# Revit family: 2-5104-24 Apollo
name_source: partatom
category: Lighting Fixtures
revit_build: Autodesk Revit LT 2014 (Build: 20130308_1515(x64)
units: mm (PartAtom-declared; Revit-internal decimal feet)

## types (1)
- 2-5104-24 Apollo
    ADA Compliant = Yes
    Apparent Load = 31 VA
    Ballast  Manufacturer = Antron Electronics
    Color Filter = 16777215
    Default Elevation = 4' - 0"
    Description = 24 1/4" Vanity
    Diffuser = Matte White Acrylic
    Dimming Lamp Color Temperature Shift = <None>
    Emit Shape Visible in Rendering = No
    Emit from Rectangle Length = 4' - 0"
    Emit from Rectangle Width = 2' - 0"
    Fixture Height = 0' - 4 1/2"
    Fixture Length = 2' - 1 1/4"
    Input Power = 30.5W
    Input Voltage = 120V
    Junction Box = 4" Octagonal
    Lamp = 2x14W T5 linear fluorescent
    Lamp Manufacturer = Sylvania
    Manufacturer = Oxygen Lighting
    Metal Finish = Satin Nickel
    Model = 2-5104-24
    Photometric Web File = 2-5104-24 Apollo 24    ITL77174.IES
    Product Documentation Link = http://oxygenlighting.com.s3.amazonaws.com
    Tilt Angle = 180.00°
    Type Comments = Lighting - Fluorescent
    URL = http:www//oxygenlighting.com

## geometry (parser evidence)
native form markers: Sweep x2
no freeform markers — native parametric forms only
